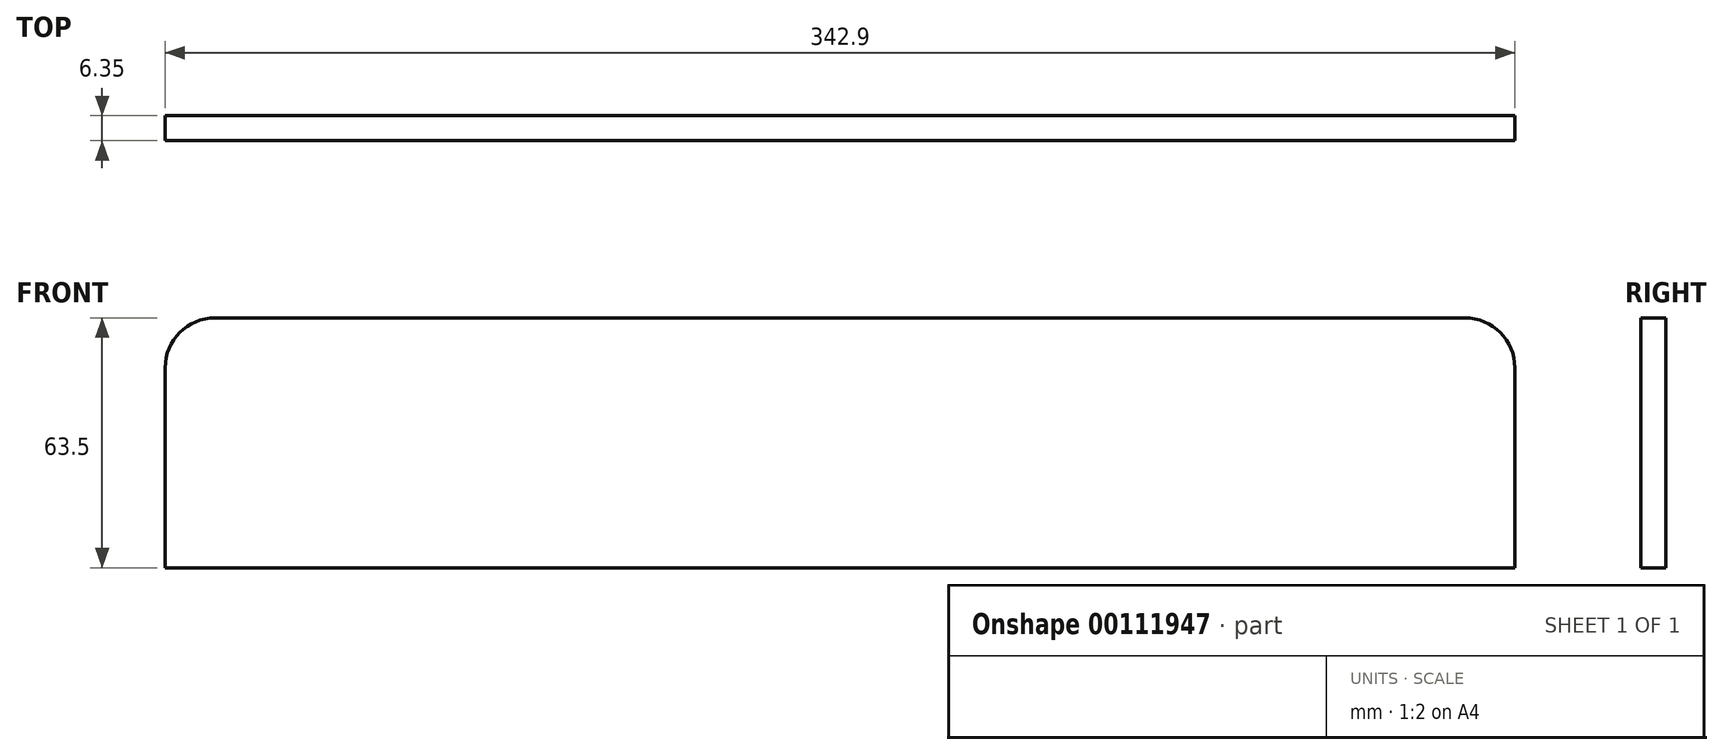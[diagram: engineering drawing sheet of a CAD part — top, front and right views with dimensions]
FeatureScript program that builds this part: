
annotation { "Feature Type Name" : "Feature", "Feature Type Description" : "" }
export const myFeature = defineFeature(function(context is Context, id is Id, definition is map)
    precondition{}
    {
        {
            var Q0;
            Q0=qCreatedBy(makeId("Front.planeOp"),FACE);
            var sketch = newSketch(context, id + "F0", { "sketchPlane" : qUnion([Q0])});
            skLineSegment(sketch, "E0.bottom", {"start": v(-171.45, 31.75) * mm, "end": v(171.45, 31.75) * mm});
            skLineSegment(sketch, "E0.top", {"start": v(-171.45, -31.75) * mm, "end": v(171.45, -31.75) * mm});
            skLineSegment(sketch, "E0.left", {"start": v(-171.45, 31.75) * mm, "end": v(-171.45, -31.75) * mm});
            skLineSegment(sketch, "E0.right", {"start": v(171.45, 31.75) * mm, "end": v(171.45, -31.75) * mm});
            skPoint(sketch, "E0.middle", {"position": v(0, 0) * mm});
            skSolve(sketch);
        }
        {
            var Q0;
            Q0=makeQuery(id+"F0.imprint","IMPRINT",FACE,{"disambiguationData":[TD([[makeQuery(id+"F0.imprint","IMPRINT",EDGE,{"derivedFrom":sQuery(id+"F0.wireOp",EDGE,"E0.bottom")}),-1.0]])]});
            extrude(context, id + "F1", {"entities" : qUnion([Q0]), "depth" : 6.35 * mm});
        }
        {
            var Q0;
            Q0=makeQuery(id+"F1.opExtrude","SWEPT_EDGE",EDGE,{"disambiguationData":[OSD([sQuery(id+"F0.wireOp",EDGE,"E0.bottom"),sQuery(id+"F0.wireOp",EDGE,"E0.left")])]});
            var Q1;
            Q1=makeQuery(id+"F1.opExtrude","SWEPT_EDGE",EDGE,{"disambiguationData":[OSD([sQuery(id+"F0.wireOp",EDGE,"E0.bottom"),sQuery(id+"F0.wireOp",EDGE,"E0.right")])]});
            fillet(context, id + "F2", {"entities" : qUnion([Q0, Q1]), "radius" : 12.7 * mm, "tangentPropagation" : true, "allowEdgeOverflow" : false});
        }
    });
